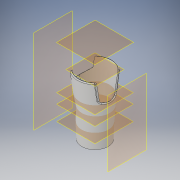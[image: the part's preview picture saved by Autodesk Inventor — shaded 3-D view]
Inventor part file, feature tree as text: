
AUTODESK INVENTOR PART (.ipt)
format: ipt  version: 2019 (Build 230136000, 136)  size: 461,824 bytes
history: native  units: mm
features: sketch x7, plane x7, fillet x3, extrude x2, loft x1, shell x1
ambient origin geometry x8: Origin, YZ Plane, XZ Plane, XY Plane, X Axis, Y Axis, Z Axis, Center Point
bodies: Solid1 (feature_tree)
feature tree (21):
  sketch  "Sketch1"  dims[d0=66.0mm d1=150.0mm d2=87.0mm]
  plane  "Work Plane1"
  sketch  "Sketch2"  dims[d3=75.0mm d4=71.0mm]
  plane  "Work Plane2"
  sketch  "Sketch3"  dims[d5=100.0mm d6=77.0mm d7=37.5mm d8=68.25mm d9=0.0mm d10=90.0deg]
  plane  "Work Plane3"
  sketch  "Sketch4"  dims[d11=0.0mm d12=90.0deg]
  plane  "Work Plane4"
  loft  "Loft1"
  shell  "Shell1"  Thickness=87.0mm
  plane  "Work Plane5"
  sketch  "Sketch6"  dims[d15=0.0mm d16=90.0deg]
  plane  "Work Plane6"
  extrude  "Extrusion1"  Depth=71.0mm
  extrude  "Extrusion2"  Depth=77.0mm
  fillet  "Fillet1"  Radius=37.5mm
  fillet  "Fillet2"  Radius=68.25mm
  fillet  "Fillet3"  [1 undecoded]
  plane  "Work Plane7"
  sketch  "Sketch5"  dims[d13=0.0mm d14=90.0deg]
  sketch  "Sketch7"  dims[d17=0.0mm d18=90.0deg d19=3.0mm d20=80.0mm d22=-104.75mm d23=75.25mm d24=0.0mm d25=49.75mm d26=0.0mm d27=2.0mm d28=2.0mm d29=2.0mm d30=208.75mm]
note: 1 required parameter value undecoded (feature->parameter linkage not recoverable at this tier; creation-order binding heuristic only, values carry confidence <= 0.55)
